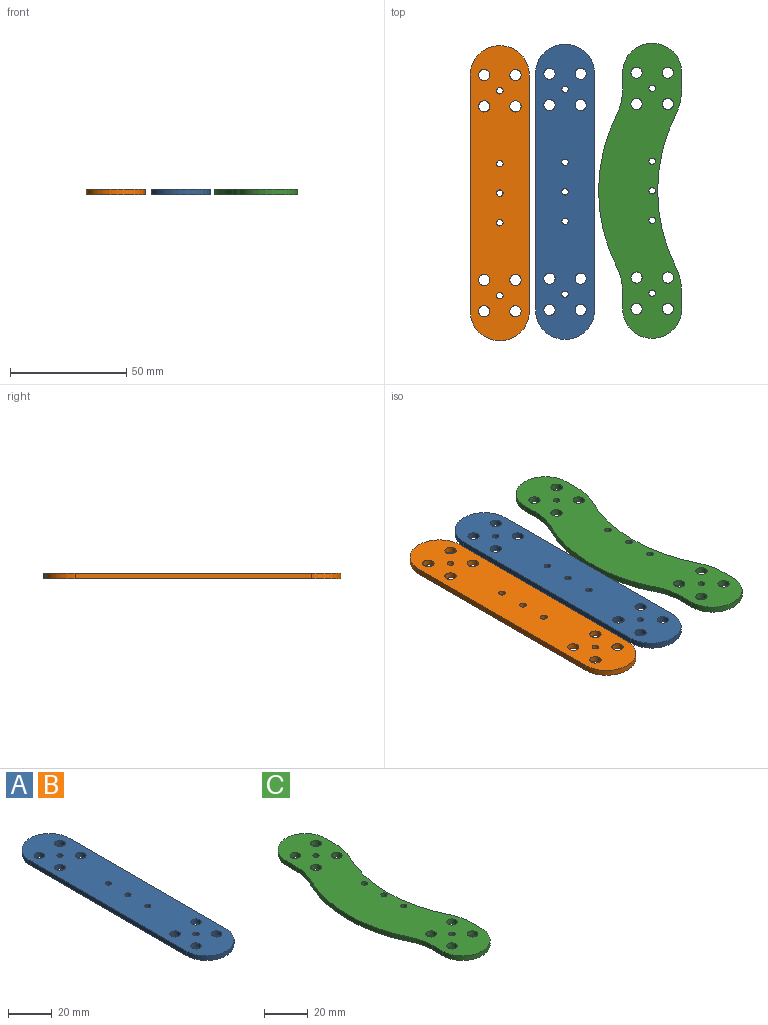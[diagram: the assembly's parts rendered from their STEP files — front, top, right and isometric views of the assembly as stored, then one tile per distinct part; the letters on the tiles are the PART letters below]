
ASSEMBLY  parts=3 mates=2
PART A: 19 faces, bbox 25.4x127x2.5 mm
  f0: plane 127x25.4mm, normal (0,0,1), area 2910.4mm2, adj f2,f3,f4,f5,f6,f7,f8,f9
  f1: plane 127x25.4mm, normal (0,0,-1), area 2910.4mm2, adj f2,f3,f4,f5,f6,f7,f8,f9
  f2: cylinder r=12.7mm len=25.4mm, axis (0,0,-1), area 101.3mm2, adj f0,f1,f3,f6
  f3: plane 101.6x2.54mm, normal (-1,0,0), area 258.1mm2, adj f0,f1,f2,f4
  f4: cylinder r=12.7mm len=25.4mm, axis (0,0,-1), area 101.3mm2, adj f0,f1,f3,f6
  f5: cylinder r=2.41mm len=4.83mm, axis (0,0,-1), area 38.5mm2, adj f0,f1
  f6: plane 101.6x2.54mm, normal (1,0,0), area 258.1mm2, adj f0,f1,f2,f4
  f7: cylinder r=2.41mm len=4.83mm, axis (0,0,-1), area 38.5mm2, adj f0,f1
  f8: cylinder r=2.41mm len=4.83mm, axis (0,0,-1), area 38.5mm2, adj f0,f1
  f9: cylinder r=2.41mm len=4.83mm, axis (0,0,-1), area 38.5mm2, adj f0,f1
  f10: cylinder r=2.41mm len=4.83mm, axis (0,0,-1), area 38.5mm2, adj f0,f1
  f11: cylinder r=2.41mm len=4.83mm, axis (0,0,-1), area 38.5mm2, adj f0,f1
  f12: cylinder r=2.41mm len=4.83mm, axis (0,0,-1), area 38.5mm2, adj f0,f1
  f13: cylinder r=2.41mm len=4.83mm, axis (0,0,-1), area 38.5mm2, adj f0,f1
  f14: cylinder r=1.4mm len=2.79mm, axis (0,0,1), area 22.3mm2, adj f0,f1
  f15: cylinder r=1.4mm len=2.79mm, axis (0,0,1), area 22.3mm2, adj f0,f1
  f16: cylinder r=1.4mm len=2.79mm, axis (0,0,1), area 22.3mm2, adj f0,f1
  f17: cylinder r=1.4mm len=2.79mm, axis (0,0,1), area 22.3mm2, adj f0,f1
  f18: cylinder r=1.4mm len=2.79mm, axis (0,0,1), area 22.3mm2, adj f0,f1
PART B: same geometry as A
PART C: 27 faces, bbox 35.8x127x2.5 mm
  f0: plane 127x35.77mm, normal (0,0,1), area 2910.4mm2, adj f2,f3,f4,f5,f6,f7,f8,f9
  f1: plane 127x35.77mm, normal (0,0,-1), area 2910.4mm2, adj f2,f3,f4,f5,f6,f7,f8,f9
  f2: cylinder r=72.39mm len=64.88mm, axis (0,0,-1), area 170.9mm2, adj f0,f1,f23,f24
  f3: plane 6.97x2.54mm, normal (-1,0,0), area 17.7mm2, adj f0,f1,f4,f24
  f4: cylinder r=12.7mm len=25.4mm, axis (0,0,-1), area 101.3mm2, adj f0,f1,f3,f5
  f5: plane 6.97x2.54mm, normal (1,0,0), area 17.7mm2, adj f0,f1,f4,f26
  f6: cylinder r=72.39mm len=64.88mm, axis (0,0,-1), area 170.9mm2, adj f0,f1,f25,f26
  f7: plane 6.97x2.54mm, normal (1,0,0), area 17.7mm2, adj f0,f1,f8,f25
  f8: cylinder r=12.7mm len=25.4mm, axis (0,0,-1), area 101.3mm2, adj f0,f1,f7,f16
  f9: cylinder r=2.41mm len=4.83mm, axis (0,0,-1), area 38.5mm2, adj f0,f1
  f10: cylinder r=2.41mm len=4.83mm, axis (0,0,-1), area 38.5mm2, adj f0,f1
  f11: cylinder r=2.41mm len=4.83mm, axis (0,0,-1), area 38.5mm2, adj f0,f1
  f12: cylinder r=2.41mm len=4.83mm, axis (0,0,-1), area 38.5mm2, adj f0,f1
  f13: cylinder r=2.41mm len=4.83mm, axis (0,0,-1), area 38.5mm2, adj f0,f1
  f14: cylinder r=2.41mm len=4.83mm, axis (0,0,-1), area 38.5mm2, adj f0,f1
  f15: cylinder r=2.41mm len=4.83mm, axis (0,0,-1), area 38.5mm2, adj f0,f1
  f16: plane 6.97x2.54mm, normal (-1,0,0), area 17.7mm2, adj f0,f1,f8,f23
  f17: cylinder r=2.41mm len=4.83mm, axis (0,0,-1), area 38.5mm2, adj f0,f1
  f18: cylinder r=1.4mm len=2.79mm, axis (0,0,1), area 22.3mm2, adj f0,f1
  f19: cylinder r=1.4mm len=2.79mm, axis (0,0,1), area 22.3mm2, adj f0,f1
  f20: cylinder r=1.4mm len=2.79mm, axis (0,0,1), area 22.3mm2, adj f0,f1
  f21: cylinder r=1.4mm len=2.79mm, axis (0,0,1), area 22.3mm2, adj f0,f1
  f22: cylinder r=1.4mm len=2.79mm, axis (0,0,1), area 22.3mm2, adj f0,f1
  f23: cylinder r=25.4mm len=11.38mm, axis (0,0,-1), area 30mm2, adj f0,f1,f2,f16
  f24: cylinder r=25.4mm len=11.38mm, axis (0,0,-1), area 30mm2, adj f0,f1,f2,f3
  f25: cylinder r=25.4mm len=11.38mm, axis (0,0,-1), area 30mm2, adj f0,f1,f6,f7
  f26: cylinder r=25.4mm len=11.38mm, axis (0,0,-1), area 30mm2, adj f0,f1,f5,f6
PLACE A t=(-58.25,4.1,1.95)mm
PLACE B t=(-86.32,3.51,1.95)mm
PLACE C t=(-20.78,4.55,1.95)mm
MATE planar B.f16 <-> A.f14  axis (0,0,1) through (-86.32,3.51,4.49)mm
MATE planar C.f0 <-> A.f16  axis (0,0,1) through (-25.41,4.55,4.49)mm
